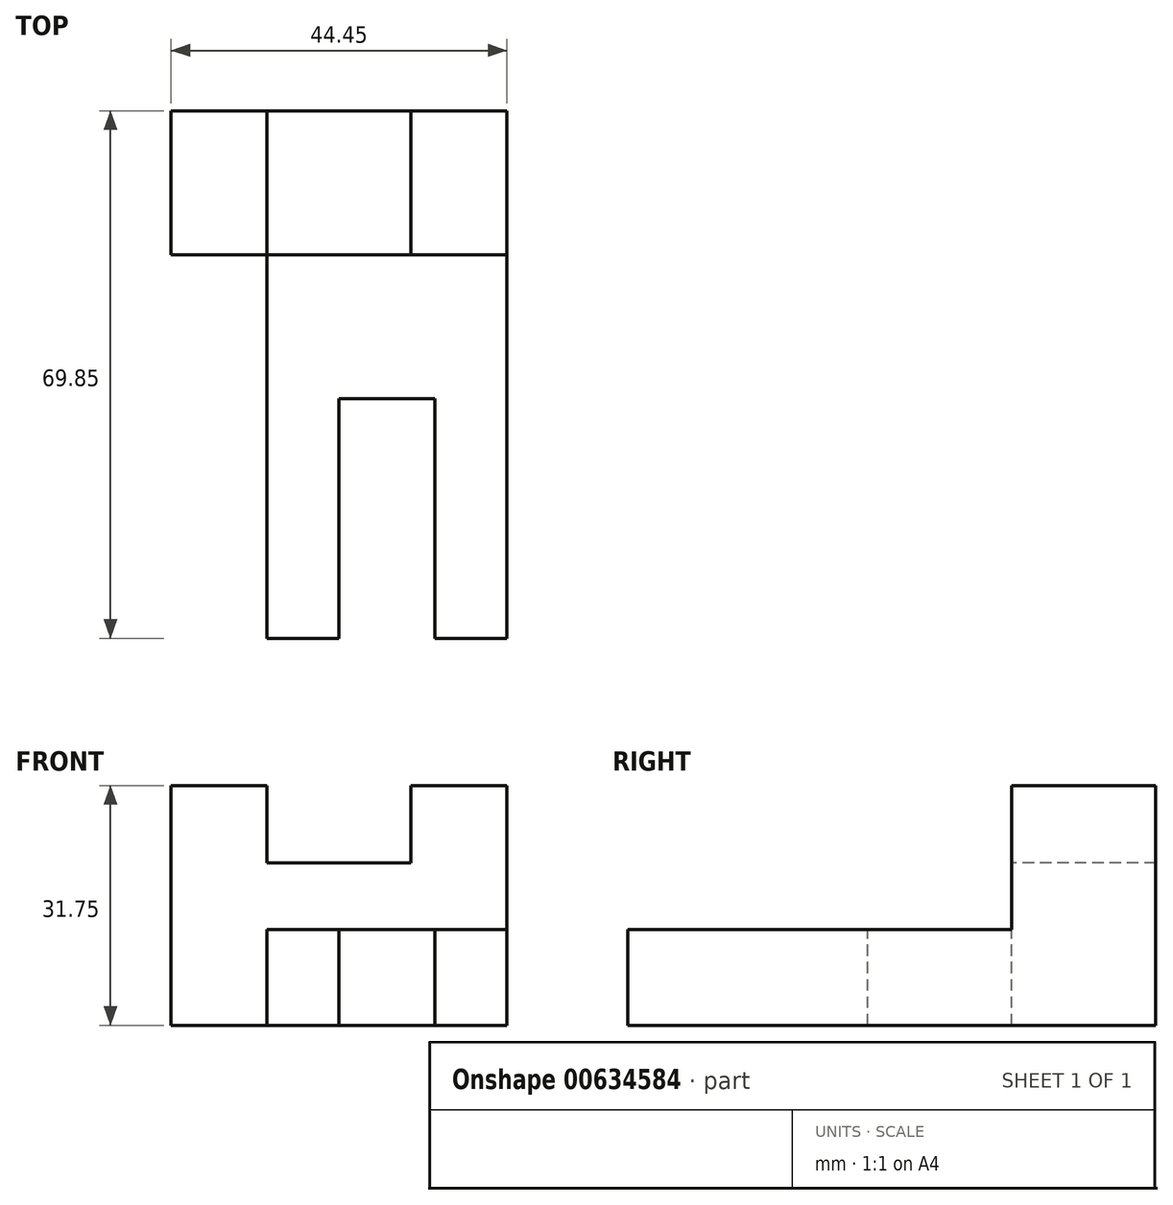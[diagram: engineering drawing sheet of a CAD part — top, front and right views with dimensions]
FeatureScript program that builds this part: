
annotation { "Feature Type Name" : "Feature", "Feature Type Description" : "" }
export const myFeature = defineFeature(function(context is Context, id is Id, definition is map)
    precondition{}
    {
        {
            var Q0;
            Q0=qCreatedBy(makeId("Front.planeOp"),FACE);
            var sketch = newSketch(context, id + "F0", { "sketchPlane" : qUnion([Q0])});
            skLineSegment(sketch, "E0", {"start": v(-44.45, 0) * mm, "end": v(-44.45, 31.75) * mm});
            skLineSegment(sketch, "E1", {"start": v(-44.45, 31.75) * mm, "end": v(0, 31.75) * mm});
            skLineSegment(sketch, "E2", {"start": v(0, 31.75) * mm, "end": v(0, 0) * mm});
            skLineSegment(sketch, "E3", {"start": v(0, 0) * mm, "end": v(-44.45, 0) * mm});
            skSolve(sketch);
        }
        {
            var Q0;
            Q0 = qSketchRegion(id + "F0", true);
            extrude(context, id + "F1", {"entities" : qUnion([Q0]), "depth" : 19.05 * mm, "offsetDistance" : 25.4 * mm});
        }
        {
            var Q0;
            Q0=makeQuery(id+"F1.opExtrude","CAP_FACE",FACE,{"disambiguationData":[OSD([sQuery(id+"F0.wireOp",EDGE,"E0"),sQuery(id+"F0.wireOp",EDGE,"E1"),sQuery(id+"F0.wireOp",EDGE,"E2"),sQuery(id+"F0.wireOp",EDGE,"E3")])],"isStart":false});
            var sketch = newSketch(context, id + "F2", { "sketchPlane" : qUnion([Q0])});
            skLineSegment(sketch, "E4", {"start": v(-31.75, 31.75) * mm, "end": v(-31.75, 21.5) * mm});
            skLineSegment(sketch, "E5", {"start": v(-31.75, 21.5) * mm, "end": v(-12.7, 21.5) * mm});
            skLineSegment(sketch, "E6", {"start": v(-12.7, 21.5) * mm, "end": v(-12.7, 31.75) * mm});
            skSolve(sketch);
        }
        {
            var Q0;
            Q0 = qSketchRegion(id + "F2", true);
            var Q1;
            {var subQ0=sQuery(id+"F2.wireOp",EDGE,"E4");Q1=makeQuery(id+"F2.imprint","IMPRINT",FACE,{"disambiguationData":[TD([[makeQuery(id+"F2.imprint","IMPRINT",EDGE,{"derivedFrom":subQ0}),1.0]])]});}
            extrude(context, id + "F3", {"entities" : qUnion([Q0, Q1]), "operationType" : NewBodyOperationType.REMOVE, "oppositeDirection" : true, "depth" : 25.4 * mm, "offsetDistance" : 25.4 * mm});
        }
        {
            var Q0;
            Q0=makeQuery(id+"F1.opExtrude","CAP_FACE",FACE,{"disambiguationData":[OSD([sQuery(id+"F0.wireOp",EDGE,"E0"),sQuery(id+"F0.wireOp",EDGE,"E1"),sQuery(id+"F0.wireOp",EDGE,"E2"),sQuery(id+"F0.wireOp",EDGE,"E3")])],"isStart":false});
            var sketch = newSketch(context, id + "F4", { "sketchPlane" : qUnion([Q0])});
            skLineSegment(sketch, "E7", {"start": v(-31.75, 0) * mm, "end": v(-31.75, 12.7) * mm});
            skLineSegment(sketch, "E8", {"start": v(-31.75, 12.7) * mm, "end": v(0, 12.7) * mm});
            skLineSegment(sketch, "E9", {"start": v(0, 12.7) * mm, "end": v(0, 0) * mm});
            skLineSegment(sketch, "E10", {"start": v(0, 0) * mm, "end": v(-31.75, 0) * mm});
            skSolve(sketch);
        }
        {
            var Q0;
            Q0 = qSketchRegion(id + "F4", true);
            extrude(context, id + "F5", {"entities" : qUnion([Q0]), "operationType" : NewBodyOperationType.ADD, "depth" : 50.8 * mm, "offsetDistance" : 25.4 * mm});
        }
        {
            var Q0;
            Q0=makeQuery(id+"F5.opExtrude","CAP_FACE",FACE,{"disambiguationData":[OSD([sQuery(id+"F4.wireOp",EDGE,"E7"),sQuery(id+"F4.wireOp",EDGE,"E8"),sQuery(id+"F4.wireOp",EDGE,"E9"),sQuery(id+"F4.wireOp",EDGE,"E10")])],"isStart":false});
            var sketch = newSketch(context, id + "F6", { "sketchPlane" : qUnion([Q0])});
            skLineSegment(sketch, "E11", {"start": v(-22.23, 0) * mm, "end": v(-22.23, 12.7) * mm});
            skLineSegment(sketch, "E12", {"start": v(-9.53, 0) * mm, "end": v(-9.53, 12.7) * mm});
            skSolve(sketch);
        }
        {
            var Q0;
            Q0=makeQuery(id+"F5.opExtrude","SWEPT_FACE",FACE,{"disambiguationData":[OSD([sQuery(id+"F4.wireOp",EDGE,"E8")])]});
            var sketch = newSketch(context, id + "F7", { "sketchPlane" : qUnion([Q0])});
            skLineSegment(sketch, "E13", {"start": v(-22.22, -69.85) * mm, "end": v(-22.23, -38.1) * mm});
            skLineSegment(sketch, "E14", {"start": v(-9.53, -69.85) * mm, "end": v(-9.53, -38.1) * mm});
            skLineSegment(sketch, "E15", {"start": v(-9.53, -38.1) * mm, "end": v(-22.23, -38.1) * mm});
            skSolve(sketch);
        }
        {
            var Q0;
            Q0 = qSketchRegion(id + "F7", true);
            var Q1;
            {var subQ0=sQuery(id+"F7.wireOp",EDGE,"E13");Q1=makeQuery(id+"F7.imprint","IMPRINT",FACE,{"disambiguationData":[TD([[makeQuery(id+"F7.imprint","IMPRINT",EDGE,{"derivedFrom":subQ0}),-1.0]])]});}
            extrude(context, id + "F8", {"entities" : qUnion([Q0, Q1]), "operationType" : NewBodyOperationType.REMOVE, "oppositeDirection" : true, "depth" : 25.4 * mm, "offsetDistance" : 25.4 * mm});
        }
        {
            var Q0;
            {var subQ0=sQuery(id+"F6.wireOp",EDGE,"E11");Q0=makeQuery(id+"F6.imprint","IMPRINT",FACE,{"disambiguationData":[TD([[makeQuery(id+"F6.imprint","IMPRINT",EDGE,{"derivedFrom":subQ0}),-1.0]])]});}
            extrude(context, id + "F9", {"entities" : qUnion([Q0]), "operationType" : NewBodyOperationType.REMOVE, "oppositeDirection" : true, "depth" : 25.4 * mm, "offsetDistance" : 25.4 * mm});
        }
    });
